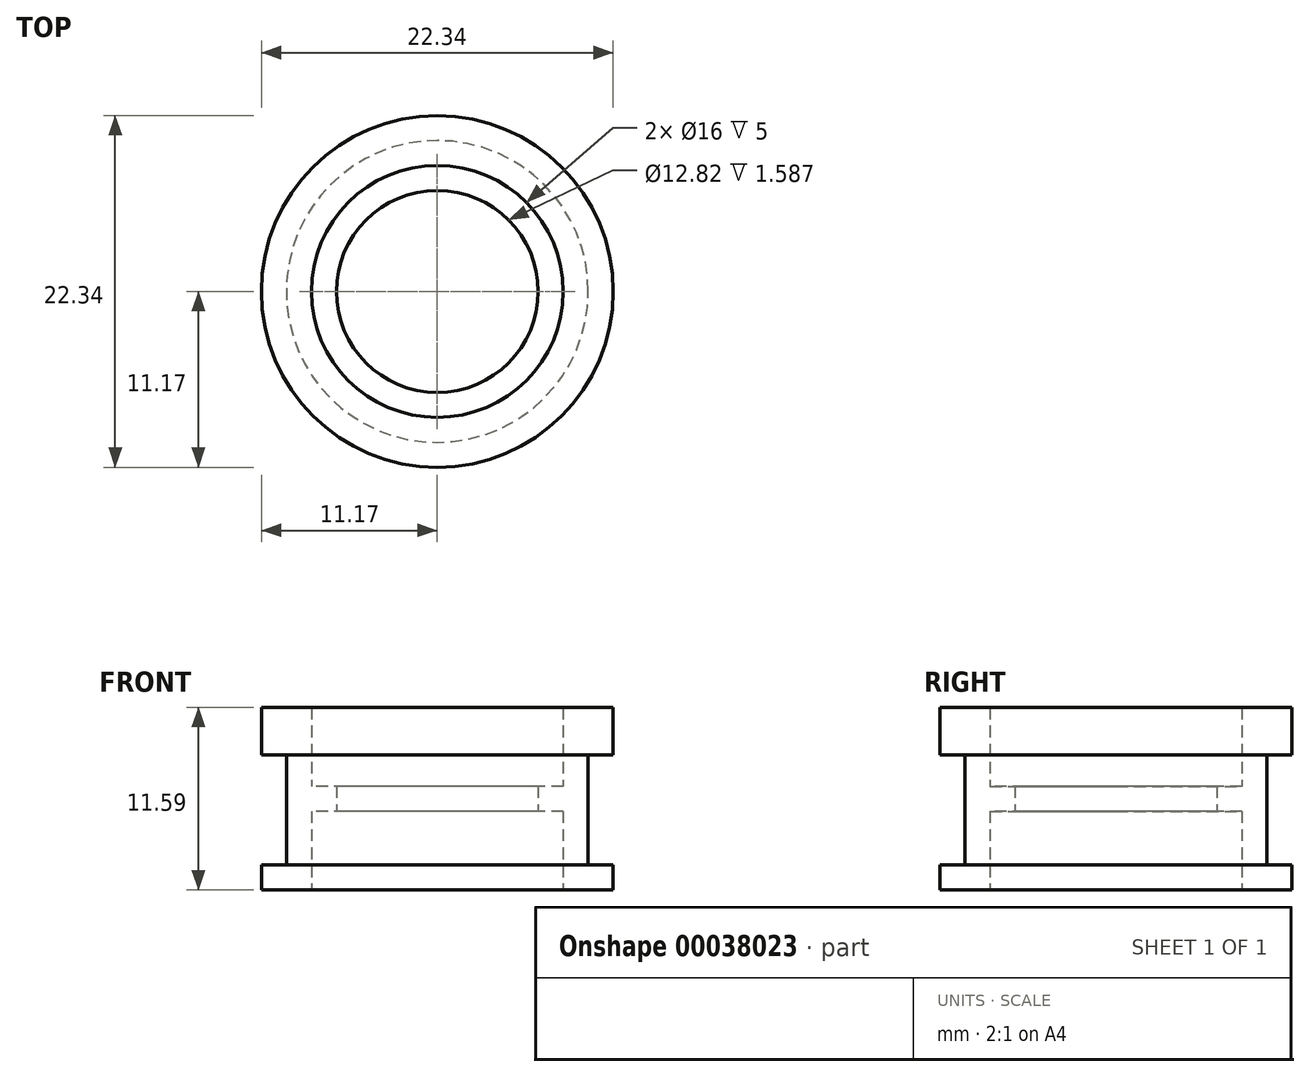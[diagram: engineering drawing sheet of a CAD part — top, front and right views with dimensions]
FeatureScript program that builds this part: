
annotation { "Feature Type Name" : "Feature", "Feature Type Description" : "" }
export const myFeature = defineFeature(function(context is Context, id is Id, definition is map)
    precondition{}
    {
        {
            var Q0;
            Q0=qCreatedBy(makeId("Top.planeOp"),FACE);
            var sketch = newSketch(context, id + "F0", { "sketchPlane" : qUnion([Q0])});
            skCircle(sketch, "E0", {"center": v(0, 0) * mm, "radius": 11.17 * mm});
            skCircle(sketch, "E1", {"center": v(0, 0) * mm, "radius": 8 * mm});
            skSolve(sketch);
        }
        {
            var Q0;
            Q0 = qSketchRegion(id + "F0", true);
            extrude(context, id + "F1", {"entities" : qUnion([Q0]), "depth" : 1.59 * mm});
        }
        {
            var Q0;
            Q0=makeQuery(id+"F1.opExtrude","CAP_FACE",FACE,{"disambiguationData":[OSD([sQuery(id+"F0.wireOp",EDGE,"E0"),sQuery(id+"F0.wireOp",EDGE,"E1")])],"isStart":false});
            var sketch = newSketch(context, id + "F2", { "sketchPlane" : qUnion([Q0])});
            skCircle(sketch, "E2", {"center": v(0, 0) * mm, "radius": 8 * mm});
            skCircle(sketch, "E3", {"center": v(0, 0) * mm, "radius": 9.59 * mm});
            skSolve(sketch);
        }
        {
            var Q0;
            Q0 = qSketchRegion(id + "F2", true);
            extrude(context, id + "F3", {"entities" : qUnion([Q0]), "operationType" : NewBodyOperationType.ADD, "depth" : 3.41 * mm});
        }
        {
            var Q0;
            Q0=makeQuery(id+"F3.opExtrude","CAP_FACE",FACE,{"disambiguationData":[OSD([sQuery(id+"F2.wireOp",EDGE,"E2"),sQuery(id+"F2.wireOp",EDGE,"E3")])],"isStart":false});
            var sketch = newSketch(context, id + "F4", { "sketchPlane" : qUnion([Q0])});
            skCircle(sketch, "E4", {"center": v(0, 0) * mm, "radius": 9.59 * mm});
            skCircle(sketch, "E5", {"center": v(0, 0) * mm, "radius": 6.41 * mm});
            skSolve(sketch);
        }
        {
            var Q0;
            Q0 = qSketchRegion(id + "F4", true);
            extrude(context, id + "F5", {"entities" : qUnion([Q0]), "operationType" : NewBodyOperationType.ADD, "depth" : 1.59 * mm});
        }
        {
            var Q0;
            Q0=makeQuery(id+"F5.opExtrude","CAP_FACE",FACE,{"disambiguationData":[OSD([sQuery(id+"F4.wireOp",EDGE,"E4"),sQuery(id+"F4.wireOp",EDGE,"E5")])],"isStart":false});
            var sketch = newSketch(context, id + "F6", { "sketchPlane" : qUnion([Q0])});
            skCircle(sketch, "E6", {"center": v(0, 0) * mm, "radius": 8 * mm});
            skCircle(sketch, "E7", {"center": v(0, 0) * mm, "radius": 9.59 * mm});
            skSolve(sketch);
        }
        {
            var Q0;
            Q0 = qSketchRegion(id + "F6", true);
            extrude(context, id + "F7", {"entities" : qUnion([Q0]), "operationType" : NewBodyOperationType.ADD, "depth" : 2 * mm});
        }
        {
            var Q0;
            Q0=makeQuery(id+"F7.opExtrude","CAP_FACE",FACE,{"disambiguationData":[OSD([sQuery(id+"F6.wireOp",EDGE,"E6"),sQuery(id+"F6.wireOp",EDGE,"E7")])],"isStart":false});
            var sketch = newSketch(context, id + "F8", { "sketchPlane" : qUnion([Q0])});
            skCircle(sketch, "E8", {"center": v(0, 0) * mm, "radius": 11.17 * mm});
            skCircle(sketch, "E9", {"center": v(0, 0) * mm, "radius": 8 * mm});
            skSolve(sketch);
        }
        {
            var Q0;
            Q0 = qSketchRegion(id + "F8", true);
            extrude(context, id + "F9", {"entities" : qUnion([Q0]), "operationType" : NewBodyOperationType.ADD, "depth" : 3 * mm});
        }
    });
